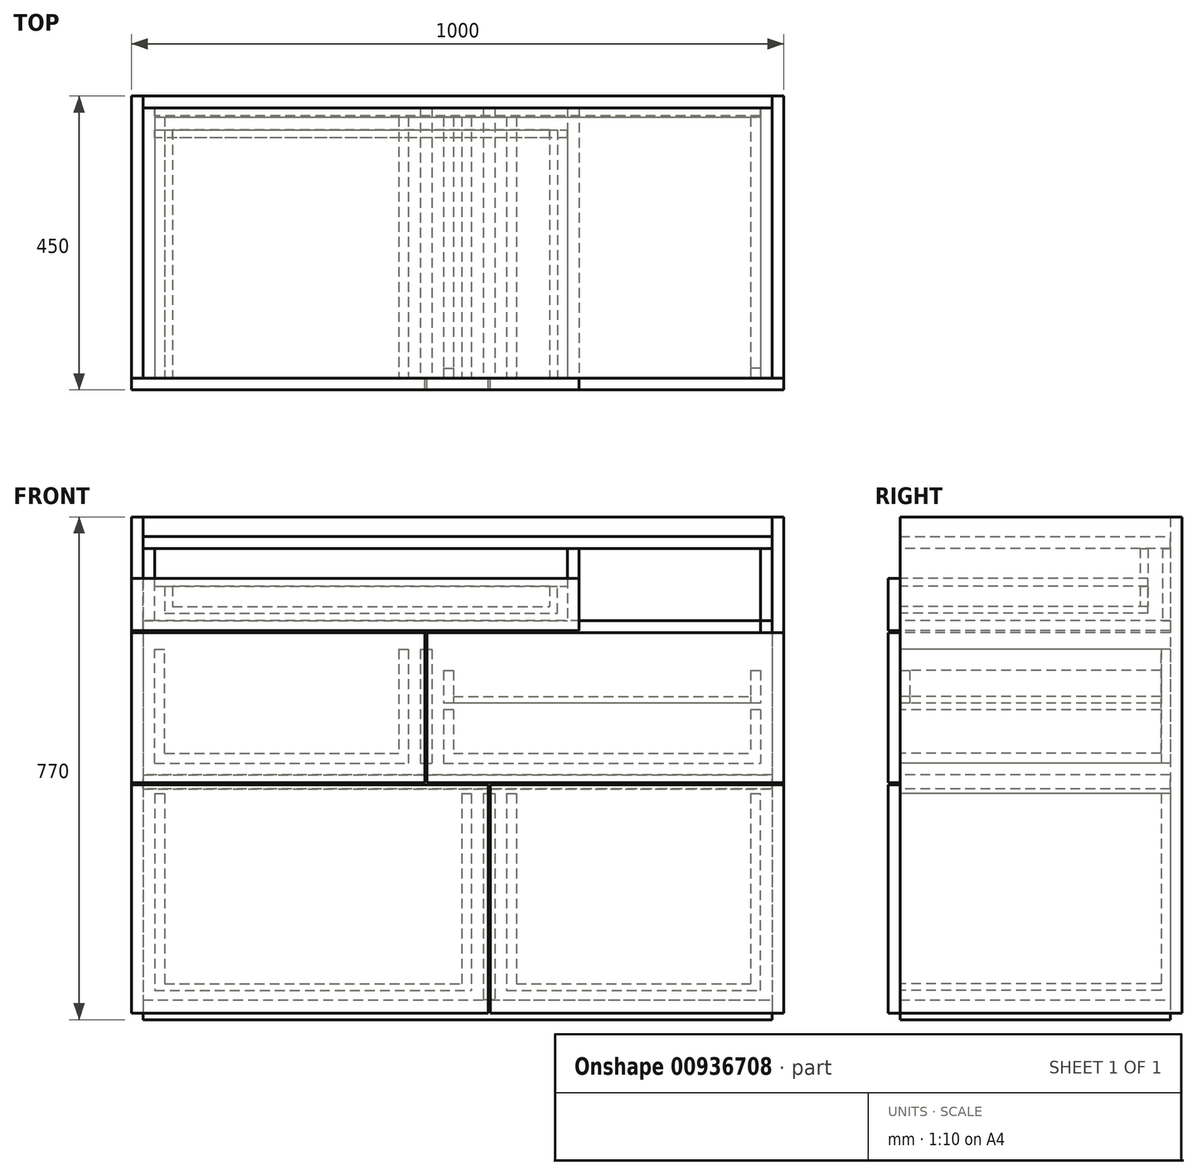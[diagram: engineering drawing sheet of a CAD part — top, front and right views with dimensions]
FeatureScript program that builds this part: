
annotation { "Feature Type Name" : "Feature", "Feature Type Description" : "" }
export const myFeature = defineFeature(function(context is Context, id is Id, definition is map)
    precondition{}
    {
        {
            var Q0;
            Q0=qCreatedBy(makeId("Top.planeOp"),FACE);
            var sketch = newSketch(context, id + "F0", { "sketchPlane" : qUnion([Q0])});
            skLineSegment(sketch, "E0.bottom", {"start": v(0, 0) * mm, "end": v(1000, 0) * mm});
            skLineSegment(sketch, "E0.top", {"start": v(0, 432) * mm, "end": v(1000, 432) * mm});
            skLineSegment(sketch, "E0.left", {"start": v(0, 0) * mm, "end": v(0, 432) * mm});
            skLineSegment(sketch, "E0.right", {"start": v(1000, 0) * mm, "end": v(1000, 432) * mm});
            skLineSegment(sketch, "E1.0", {"start": v(18, 0) * mm, "end": v(18, 432) * mm});
            skLineSegment(sketch, "E2", {"start": v(500, 455.77) * mm, "end": v(500, 504.04) * mm, "construction": true});
            skPoint(sketch, "E2.startSnap0", {"position": v(500, 432) * mm});
            skLineSegment(sketch, "E3.MirrorCS", {"start": v(982, 0) * mm, "end": v(982, 432) * mm});
            skLineSegment(sketch, "E4", {"start": v(1025.2, 216) * mm, "end": v(1096.23, 216) * mm, "construction": true});
            skPoint(sketch, "E4.startSnap0", {"position": v(1000, 216) * mm});
            skLineSegment(sketch, "E5.0", {"start": v(0, 414) * mm, "end": v(1000, 414) * mm});
            skSolve(sketch);
        }
        {
            var Q0;
            {var subQ0=sQuery(id+"F0.wireOp",EDGE,"E0.left");var subQ1=sQuery(id+"F0.wireOp",EDGE,"E0.bottom");var subQ2=makeQuery(id+"F0.imprint","INTERSECT",VERTEX,{"derivedFrom":[subQ1,subQ0]});Q0=makeQuery(id+"F0.imprint","IMPRINT",FACE,{"disambiguationData":[TD([[makeQuery(id+"F0.imprint","IMPRINT",EDGE,{"disambiguationData":[TD([[subQ2,-1.0]])],"derivedFrom":subQ1}),1.0]])]});}
            var Q1;
            {var subQ0=sQuery(id+"F0.wireOp",EDGE,"E0.left");var subQ1=sQuery(id+"F0.wireOp",EDGE,"E0.top");var subQ2=makeQuery(id+"F0.imprint","INTERSECT",VERTEX,{"derivedFrom":[subQ1,subQ0]});Q1=makeQuery(id+"F0.imprint","IMPRINT",FACE,{"disambiguationData":[TD([[makeQuery(id+"F0.imprint","IMPRINT",EDGE,{"disambiguationData":[TD([[subQ2,-1.0]])],"derivedFrom":subQ1}),-1.0]])]});}
            var Q2;
            {var subQ0=sQuery(id+"F0.wireOp",EDGE,"E0.right");var subQ1=sQuery(id+"F0.wireOp",EDGE,"E0.bottom");var subQ2=makeQuery(id+"F0.imprint","INTERSECT",VERTEX,{"derivedFrom":[subQ1,subQ0]});Q2=makeQuery(id+"F0.imprint","IMPRINT",FACE,{"disambiguationData":[TD([[makeQuery(id+"F0.imprint","IMPRINT",EDGE,{"disambiguationData":[TD([[subQ2,1.0]])],"derivedFrom":subQ1}),1.0]])]});}
            var Q3;
            {var subQ0=sQuery(id+"F0.wireOp",EDGE,"E0.right");var subQ1=sQuery(id+"F0.wireOp",EDGE,"E0.top");var subQ2=makeQuery(id+"F0.imprint","INTERSECT",VERTEX,{"derivedFrom":[subQ1,subQ0]});Q3=makeQuery(id+"F0.imprint","IMPRINT",FACE,{"disambiguationData":[TD([[makeQuery(id+"F0.imprint","IMPRINT",EDGE,{"disambiguationData":[TD([[subQ2,1.0]])],"derivedFrom":subQ1}),-1.0]])]});}
            extrude(context, id + "F1", {"entities" : qUnion([Q0, Q1, Q2, Q3]), "depth" : 760 * mm, "offsetDistance" : 25 * mm});
        }
        {
            var Q0;
            {var subQ0=sQuery(id+"F0.wireOp",EDGE,"E1.0");var subQ1=sQuery(id+"F0.wireOp",EDGE,"E0.top");var subQ2=makeQuery(id+"F0.imprint","INTERSECT",VERTEX,{"derivedFrom":[subQ1,subQ0]});Q0=makeQuery(id+"F0.imprint","IMPRINT",FACE,{"disambiguationData":[TD([[makeQuery(id+"F0.imprint","IMPRINT",EDGE,{"disambiguationData":[TD([[subQ2,-1.0]])],"derivedFrom":subQ1}),-1.0]])]});}
            var Q1;
            Q1=makeQuery(id+"F1.opExtrude","CAP_FACE",FACE,{"disambiguationData":[OSD([sQuery(id+"F0.wireOp",EDGE,"E0.bottom"),sQuery(id+"F0.wireOp",EDGE,"E0.top"),sQuery(id+"F0.wireOp",EDGE,"E0.left"),sQuery(id+"F0.wireOp",EDGE,"E1.0")])],"isStart":false});
            extrude(context, id + "F2", {"entities" : qUnion([Q0]), "endBound" : BoundingType.UP_TO_SURFACE, "depth" : 25 * mm, "endBoundEntityFace" : qUnion([Q1]), "offsetDistance" : 25 * mm});
        }
        {
            var Q0;
            {var subQ0=sQuery(id+"F0.wireOp",EDGE,"E1.0");var subQ1=sQuery(id+"F0.wireOp",EDGE,"E0.bottom");var subQ2=makeQuery(id+"F0.imprint","INTERSECT",VERTEX,{"derivedFrom":[subQ1,subQ0]});Q0=makeQuery(id+"F0.imprint","IMPRINT",FACE,{"disambiguationData":[TD([[makeQuery(id+"F0.imprint","IMPRINT",EDGE,{"disambiguationData":[TD([[subQ2,-1.0]])],"derivedFrom":subQ1}),1.0]])]});}
            extrude(context, id + "F3", {"entities" : qUnion([Q0]), "depth" : 20 * mm, "offsetDistance" : 25 * mm, "hasSecondDirection" : true, "secondDirectionOppositeDirection" : true, "secondDirectionDepth" : 10 * mm});
        }
        {
            var Q0;
            Q0=makeQuery(id+"F1.opExtrude","CAP_FACE",FACE,{"disambiguationData":[OSD([sQuery(id+"F0.wireOp",EDGE,"E0.bottom"),sQuery(id+"F0.wireOp",EDGE,"E0.top"),sQuery(id+"F0.wireOp",EDGE,"E0.left"),sQuery(id+"F0.wireOp",EDGE,"E1.0")])],"isStart":false});
            var sketch = newSketch(context, id + "F4", { "sketchPlane" : qUnion([Q0])});
            skLineSegment(sketch, "E6.bottom", {"start": v(0, 432) * mm, "end": v(1000, 432) * mm});
            skLineSegment(sketch, "E6.top", {"start": v(0, 0) * mm, "end": v(1000, 0) * mm});
            skLineSegment(sketch, "E6.left", {"start": v(0, 432) * mm, "end": v(0, 0) * mm});
            skLineSegment(sketch, "E6.right", {"start": v(1000, 432) * mm, "end": v(1000, 0) * mm});
            skLineSegment(sketch, "E7.bottom", {"start": v(18, 0) * mm, "end": v(982, 0) * mm});
            skLineSegment(sketch, "E7.top", {"start": v(18, 414) * mm, "end": v(982, 414) * mm});
            skLineSegment(sketch, "E7.left", {"start": v(18, 0) * mm, "end": v(18, 414) * mm});
            skLineSegment(sketch, "E7.right", {"start": v(982, 0) * mm, "end": v(982, 414) * mm});
            skLineSegment(sketch, "E8", {"start": v(668, 414) * mm, "end": v(668, 0) * mm});
            skLineSegment(sketch, "E9", {"start": v(18, 300) * mm, "end": v(668, 300) * mm});
            skLineSegment(sketch, "E10", {"start": v(55.2, 414) * mm, "end": v(55.2, -186) * mm, "construction": true});
            skLineSegment(sketch, "E11", {"start": v(-81.86, 114) * mm, "end": v(55.2, 114) * mm, "construction": true});
            skLineSegment(sketch, "E12", {"start": v(55.2, 0) * mm, "end": v(-78.13, 0) * mm, "construction": true});
            skLineSegment(sketch, "E13", {"start": v(55.2, -186) * mm, "end": v(-68.9, -186) * mm, "construction": true});
            skSolve(sketch);
        }
        {
            var Q0;
            {var subQ0=sQuery(id+"F4.wireOp",EDGE,"E7.right");Q0=makeQuery(id+"F4.imprint","IMPRINT",FACE,{"disambiguationData":[TD([[makeQuery(id+"F4.imprint","IMPRINT",EDGE,{"derivedFrom":subQ0}),1.0]])]});}
            var Q1;
            {var subQ5=sQuery(id+"F4.wireOp",EDGE,"E9");Q1=makeQuery(id+"F4.imprint","IMPRINT",FACE,{"disambiguationData":[TD([[makeQuery(id+"F4.imprint","IMPRINT",EDGE,{"derivedFrom":subQ5}),-1.0]])]});}
            var Q2;
            {var subQ5=sQuery(id+"F4.wireOp",EDGE,"E9");Q2=makeQuery(id+"F4.imprint","IMPRINT",FACE,{"disambiguationData":[TD([[makeQuery(id+"F4.imprint","IMPRINT",EDGE,{"derivedFrom":subQ5}),1.0]])]});}
            extrude(context, id + "F5", {"entities" : qUnion([Q0, Q1, Q2]), "oppositeDirection" : true, "depth" : 18 * mm, "offsetDistance" : 25 * mm});
        }
        {
            var Q0;
            Q0=makeQuery(id+"FaU98XOoRjI6tdl_2.opExtrude","SWEPT_BODY",BODY,{"disambiguationData":[OSD([sQuery(id+"F4.wireOp",EDGE,"E7.bottom"),sQuery(id+"F4.wireOp",EDGE,"E7.top"),sQuery(id+"F4.wireOp",EDGE,"E7.left"),sQuery(id+"F4.wireOp",EDGE,"E8")])]});
            var Q1;
            Q1=makeQuery(id+"F5.opExtrude","SWEPT_BODY",BODY,{"disambiguationData":[OSD([sQuery(id+"F4.wireOp",EDGE,"E7.bottom"),sQuery(id+"F4.wireOp",EDGE,"E7.top"),sQuery(id+"F4.wireOp",EDGE,"E7.right"),sQuery(id+"F4.wireOp",EDGE,"E8")])]});
            transform(context, id + "F6", {"entities" : qUnion([Q0, Q1]), "transformType" : TransformType.TRANSLATION_3D, "dx" : 0 * mm, "dy" : 0 * mm, "dz" : -30 * mm, "makeCopy" : false});
        }
        {
            var Q0;
            {var subQ0=sQuery(id+"F0.wireOp",EDGE,"E0.bottom");Q0=makeQuery(id+"F1.opExtrude","SWEPT_FACE",FACE,{"disambiguationData":[OSD([subQ0]),TDD([makeQuery(id+"F0.imprint","IMPRINT",EDGE,{"disambiguationData":[TD([[makeQuery(id+"F0.imprint","INTERSECT",VERTEX,{"derivedFrom":[subQ0,sQuery(id+"F0.wireOp",EDGE,"E0.left")]}),-1.0]])],"derivedFrom":subQ0})])]});}
            var sketch = newSketch(context, id + "F7", { "sketchPlane" : qUnion([Q0])});
            skLineSegment(sketch, "E14.bottom", {"start": v(0, 730) * mm, "end": v(668, 730) * mm});
            skLineSegment(sketch, "E14.top", {"start": v(0, 586) * mm, "end": v(668, 586) * mm});
            skLineSegment(sketch, "E14.left", {"start": v(0, 730) * mm, "end": v(0, 586) * mm});
            skLineSegment(sketch, "E14.right", {"start": v(668, 730) * mm, "end": v(668, 586) * mm});
            skLineSegment(sketch, "E15.bottom", {"start": v(1000, 583) * mm, "end": v(756, 583) * mm});
            skLineSegment(sketch, "E15.top", {"start": v(1000, 353) * mm, "end": v(756, 353) * mm});
            skLineSegment(sketch, "E15.left", {"start": v(1000, 583) * mm, "end": v(1000, 353) * mm});
            skLineSegment(sketch, "E15.right", {"start": v(756, 583) * mm, "end": v(756, 353) * mm});
            skLineSegment(sketch, "E16.bottom", {"start": v(753, 583) * mm, "end": v(453, 583) * mm});
            skLineSegment(sketch, "E16.top", {"start": v(753, 353) * mm, "end": v(453, 353) * mm});
            skLineSegment(sketch, "E16.left", {"start": v(753, 583) * mm, "end": v(753, 353) * mm});
            skLineSegment(sketch, "E16.right", {"start": v(453, 583) * mm, "end": v(453, 353) * mm});
            skLineSegment(sketch, "E17.bottom", {"start": v(450, 583) * mm, "end": v(0, 583) * mm});
            skLineSegment(sketch, "E17.top", {"start": v(450, 353) * mm, "end": v(0, 353) * mm});
            skLineSegment(sketch, "E17.left", {"start": v(450, 583) * mm, "end": v(450, 353) * mm});
            skLineSegment(sketch, "E17.right", {"start": v(0, 583) * mm, "end": v(0, 353) * mm});
            skLineSegment(sketch, "E18.bottom", {"start": v(671, 730) * mm, "end": v(1000, 730) * mm});
            skLineSegment(sketch, "E18.top", {"start": v(671, 586) * mm, "end": v(1000, 586) * mm});
            skLineSegment(sketch, "E18.left", {"start": v(671, 730) * mm, "end": v(671, 586) * mm});
            skLineSegment(sketch, "E18.right", {"start": v(1000, 730) * mm, "end": v(1000, 586) * mm});
            skLineSegment(sketch, "E19", {"start": v(668, 658) * mm, "end": v(671, 658) * mm, "construction": true});
            skLineSegment(sketch, "E20", {"start": v(1108.22, 586) * mm, "end": v(1108.22, 583) * mm, "construction": true});
            skLineSegment(sketch, "E21", {"start": v(756, 468) * mm, "end": v(753, 468) * mm, "construction": true});
            skLineSegment(sketch, "E22", {"start": v(453, 468) * mm, "end": v(450, 468) * mm, "construction": true});
            skLineSegment(sketch, "E23.bottom", {"start": v(0, 0) * mm, "end": v(244, 0) * mm});
            skLineSegment(sketch, "E23.top", {"start": v(0, 350) * mm, "end": v(244, 350) * mm});
            skLineSegment(sketch, "E23.left", {"start": v(0, 0) * mm, "end": v(0, 350) * mm});
            skLineSegment(sketch, "E23.right", {"start": v(244, 0) * mm, "end": v(244, 350) * mm});
            skLineSegment(sketch, "E24.bottom", {"start": v(247, 350) * mm, "end": v(547, 350) * mm});
            skLineSegment(sketch, "E24.top", {"start": v(247, 0) * mm, "end": v(547, 0) * mm});
            skLineSegment(sketch, "E24.left", {"start": v(247, 350) * mm, "end": v(247, 0) * mm});
            skLineSegment(sketch, "E24.right", {"start": v(547, 350) * mm, "end": v(547, 0) * mm});
            skLineSegment(sketch, "E25.bottom", {"start": v(550, 350) * mm, "end": v(1000, 350) * mm});
            skLineSegment(sketch, "E25.top", {"start": v(550, 0) * mm, "end": v(1000, 0) * mm});
            skLineSegment(sketch, "E25.left", {"start": v(550, 350) * mm, "end": v(550, 0) * mm});
            skLineSegment(sketch, "E25.right", {"start": v(1000, 350) * mm, "end": v(1000, 0) * mm});
            skLineSegment(sketch, "E26", {"start": v(122, 353) * mm, "end": v(122, 350) * mm, "construction": true});
            skPoint(sketch, "E26.startSnap0", {"position": v(122, 350) * mm});
            skLineSegment(sketch, "E27", {"start": v(244, 175) * mm, "end": v(247, 175) * mm, "construction": true});
            skLineSegment(sketch, "E28", {"start": v(550, 175) * mm, "end": v(547, 175) * mm, "construction": true});
            skLineSegment(sketch, "E29.bottom", {"start": v(671, 586) * mm, "end": v(982, 586) * mm});
            skLineSegment(sketch, "E29.top", {"start": v(671, 604) * mm, "end": v(982, 604) * mm});
            skLineSegment(sketch, "E29.left", {"start": v(671, 586) * mm, "end": v(671, 604) * mm});
            skLineSegment(sketch, "E29.right", {"start": v(982, 586) * mm, "end": v(982, 604) * mm});
            skLineSegment(sketch, "E30", {"start": v(668, 712) * mm, "end": v(0, 712) * mm});
            skLineSegment(sketch, "E31", {"start": v(450, 583) * mm, "end": v(453, 583) * mm});
            skLineSegment(sketch, "E32", {"start": v(450, 353) * mm, "end": v(453, 353) * mm});
            skLineSegment(sketch, "E33", {"start": v(547, 350) * mm, "end": v(550, 350) * mm});
            skLineSegment(sketch, "E34", {"start": v(547, 0) * mm, "end": v(550, 0) * mm});
            skLineSegment(sketch, "E35", {"start": v(753, 583) * mm, "end": v(756, 583) * mm});
            skLineSegment(sketch, "E36", {"start": v(753, 353) * mm, "end": v(756, 353) * mm});
            skLineSegment(sketch, "E37", {"start": v(244, 350) * mm, "end": v(247, 350) * mm});
            skLineSegment(sketch, "E38", {"start": v(244, 0) * mm, "end": v(247, 0) * mm});
            skLineSegment(sketch, "E39", {"start": v(0, 666) * mm, "end": v(668, 666) * mm});
            skSolve(sketch);
        }
        {
            var Q0;
            {var subQ0=sQuery(id+"F7.wireOp",EDGE,"E17.left");Q0=makeQuery(id+"F7.imprint","IMPRINT",FACE,{"disambiguationData":[TD([[makeQuery(id+"F7.imprint","IMPRINT",EDGE,{"derivedFrom":subQ0}),-1.0]])]});}
            var Q1;
            Q1=makeQuery(id+"F7.imprint","IMPRINT",FACE,{"disambiguationData":[TD([[makeQuery(id+"F7.imprint","IMPRINT",EDGE,{"derivedFrom":sQuery(id+"F7.wireOp",EDGE,"E16.bottom")}),1.0]])]});
            var Q2;
            Q2=makeQuery(id+"F7.imprint","IMPRINT",FACE,{"disambiguationData":[TD([[makeQuery(id+"F7.imprint","IMPRINT",EDGE,{"derivedFrom":sQuery(id+"F7.wireOp",EDGE,"E15.bottom")}),1.0]])]});
            var Q3;
            Q3=makeQuery(id+"F7.imprint","IMPRINT",FACE,{"disambiguationData":[TD([[makeQuery(id+"F7.imprint","IMPRINT",EDGE,{"derivedFrom":sQuery(id+"F7.wireOp",EDGE,"E25.bottom")}),-1.0]])]});
            var Q4;
            Q4=makeQuery(id+"F7.imprint","IMPRINT",FACE,{"disambiguationData":[TD([[makeQuery(id+"F7.imprint","IMPRINT",EDGE,{"derivedFrom":sQuery(id+"F7.wireOp",EDGE,"E24.bottom")}),-1.0]])]});
            var Q5;
            {var subQ3=sQuery(id+"F7.wireOp",EDGE,"E23.right");Q5=makeQuery(id+"F7.imprint","IMPRINT",FACE,{"disambiguationData":[TD([[makeQuery(id+"F7.imprint","IMPRINT",EDGE,{"derivedFrom":subQ3}),1.0]])]});}
            var Q6;
            {var subQ0=sQuery(id+"F7.wireOp",EDGE,"E17.right");Q6=makeQuery(id+"F7.imprint","IMPRINT",FACE,{"disambiguationData":[TD([[makeQuery(id+"F7.imprint","IMPRINT",EDGE,{"derivedFrom":subQ0}),1.0]])]});}
            var Q7;
            {var subQ0=sQuery(id+"F7.wireOp",EDGE,"E23.left");Q7=makeQuery(id+"F7.imprint","IMPRINT",FACE,{"disambiguationData":[TD([[makeQuery(id+"F7.imprint","IMPRINT",EDGE,{"derivedFrom":subQ0}),1.0]])]});}
            var Q8;
            {var subQ0=sQuery(id+"F7.wireOp",EDGE,"E14.right");var subQ1=sQuery(id+"F7.wireOp",EDGE,"E14.top");var subQ2=makeQuery(id+"F7.imprint","INTERSECT",VERTEX,{"derivedFrom":[subQ1,subQ0]});Q8=makeQuery(id+"F7.imprint","IMPRINT",FACE,{"disambiguationData":[TD([[makeQuery(id+"F7.imprint","IMPRINT",EDGE,{"disambiguationData":[TD([[subQ2,1.0]])],"derivedFrom":subQ0}),-1.0]])]});}
            var Q9;
            Q9=makeQuery(id+"F7.imprint","IMPRINT",FACE,{"disambiguationData":[TD([[makeQuery(id+"F7.imprint","IMPRINT",EDGE,{"derivedFrom":sQuery(id+"F7.wireOp",EDGE,"E23.right")}),-1.0]])]});
            var Q10;
            Q10=makeQuery(id+"F7.imprint","IMPRINT",FACE,{"disambiguationData":[TD([[makeQuery(id+"F7.imprint","IMPRINT",EDGE,{"derivedFrom":sQuery(id+"F7.wireOp",EDGE,"E15.right")}),-1.0]])]});
            var Q11;
            {var subQ0=sQuery(id+"F7.wireOp",EDGE,"E14.left");var subQ6=sQuery(id+"F7.wireOp",EDGE,"E39");var subQ8=makeQuery(id+"F7.imprint","INTERSECT",VERTEX,{"derivedFrom":[subQ0,subQ6]});Q11=makeQuery(id+"F7.imprint","IMPRINT",FACE,{"disambiguationData":[TD([[makeQuery(id+"F7.imprint","IMPRINT",EDGE,{"disambiguationData":[TD([[subQ8,-1.0]])],"derivedFrom":subQ6}),-1.0]])]});}
            extrude(context, id + "F8", {"entities" : qUnion([Q0, Q1, Q2, Q3, Q4, Q5, Q6, Q7, Q8, Q9, Q10, Q11]), "depth" : 18 * mm, "offsetDistance" : 25 * mm});
        }
        {
            var Q0;
            Q0=makeQuery(id+"F8.opExtrude","CAP_FACE",FACE,{"disambiguationData":[OSD([sQuery(id+"F7.wireOp",EDGE,"E14.bottom"),sQuery(id+"F7.wireOp",EDGE,"E14.top"),sQuery(id+"F7.wireOp",EDGE,"E14.left"),sQuery(id+"F7.wireOp",EDGE,"E14.right")])],"isStart":true});
            var sketch = newSketch(context, id + "F9", { "sketchPlane" : qUnion([Q0])});
            skLineSegment(sketch, "E40.bottom", {"start": v(-18, 583) * mm, "end": v(-982, 583) * mm});
            skLineSegment(sketch, "E40.top", {"start": v(-18, 565) * mm, "end": v(-982, 565) * mm});
            skLineSegment(sketch, "E40.left", {"start": v(-18, 583) * mm, "end": v(-18, 565) * mm});
            skLineSegment(sketch, "E40.right", {"start": v(-982, 583) * mm, "end": v(-982, 565) * mm});
            skLineSegment(sketch, "E41.bottom", {"start": v(-18, 365) * mm, "end": v(-982, 365) * mm});
            skLineSegment(sketch, "E41.top", {"start": v(-18, 343.75) * mm, "end": v(-982, 343.75) * mm});
            skLineSegment(sketch, "E41.left", {"start": v(-18, 365) * mm, "end": v(-18, 343.75) * mm});
            skLineSegment(sketch, "E41.right", {"start": v(-982, 365) * mm, "end": v(-982, 343.75) * mm});
            skLineSegment(sketch, "E42.bottom", {"start": v(-982, 565) * mm, "end": v(-964, 565) * mm});
            skLineSegment(sketch, "E42.top", {"start": v(-982, 365) * mm, "end": v(-964, 365) * mm});
            skLineSegment(sketch, "E42.left", {"start": v(-982, 565) * mm, "end": v(-982, 365) * mm});
            skLineSegment(sketch, "E42.right", {"start": v(-964, 565) * mm, "end": v(-964, 365) * mm});
            skLineSegment(sketch, "E43.bottom", {"start": v(-460.5, 565) * mm, "end": v(-442.5, 565) * mm});
            skLineSegment(sketch, "E43.top", {"start": v(-460.5, 365) * mm, "end": v(-442.5, 365) * mm});
            skLineSegment(sketch, "E43.left", {"start": v(-460.5, 565) * mm, "end": v(-460.5, 365) * mm});
            skLineSegment(sketch, "E43.right", {"start": v(-442.5, 565) * mm, "end": v(-442.5, 365) * mm});
            skLineSegment(sketch, "E44.bottom", {"start": v(-557.18, 343.75) * mm, "end": v(-539.18, 343.75) * mm});
            skLineSegment(sketch, "E44.top", {"start": v(-557.18, 20) * mm, "end": v(-539.18, 20) * mm});
            skLineSegment(sketch, "E44.left", {"start": v(-557.18, 343.75) * mm, "end": v(-557.18, 20) * mm});
            skLineSegment(sketch, "E44.right", {"start": v(-539.18, 343.75) * mm, "end": v(-539.18, 20) * mm});
            skLineSegment(sketch, "E45.bottom", {"start": v(-36, 343.75) * mm, "end": v(-18, 343.75) * mm});
            skLineSegment(sketch, "E45.top", {"start": v(-36, 20) * mm, "end": v(-18, 20) * mm});
            skLineSegment(sketch, "E45.left", {"start": v(-36, 343.75) * mm, "end": v(-36, 20) * mm});
            skLineSegment(sketch, "E45.right", {"start": v(-18, 343.75) * mm, "end": v(-18, 20) * mm});
            skLineSegment(sketch, "E46", {"start": v(-548.18, 289.25) * mm, "end": v(-548.18, 277.23) * mm, "construction": true});
            skPoint(sketch, "E47", {"position": v(-548.18, 20) * mm});
            skPoint(sketch, "E48", {"position": v(-27, 20) * mm});
            skPoint(sketch, "E49", {"position": v(-973, 365) * mm});
            skPoint(sketch, "E50", {"position": v(-451.5, 365) * mm});
            skLineSegment(sketch, "E51.bottom", {"start": v(-686, 712) * mm, "end": v(-668, 712) * mm});
            skLineSegment(sketch, "E51.left", {"start": v(-686, 712) * mm, "end": v(-686, 583) * mm});
            skLineSegment(sketch, "E51.right", {"start": v(-668, 712) * mm, "end": v(-668, 583) * mm});
            skPoint(sketch, "E52", {"position": v(-677, 563.5) * mm});
            skLineSegment(sketch, "E53.bottom", {"start": v(-982, 583) * mm, "end": v(-964, 583) * mm});
            skLineSegment(sketch, "E53.top", {"start": v(-982, 712) * mm, "end": v(-964, 712) * mm});
            skLineSegment(sketch, "E53.left", {"start": v(-982, 583) * mm, "end": v(-982, 712) * mm});
            skLineSegment(sketch, "E53.right", {"start": v(-964, 583) * mm, "end": v(-964, 712) * mm});
            skLineSegment(sketch, "E54.bottom", {"start": v(-36, 365) * mm, "end": v(-51, 365) * mm});
            skLineSegment(sketch, "E54.top", {"start": v(-36, 565) * mm, "end": v(-51, 565) * mm});
            skLineSegment(sketch, "E54.left", {"start": v(-36, 365) * mm, "end": v(-36, 565) * mm});
            skLineSegment(sketch, "E54.right", {"start": v(-51, 365) * mm, "end": v(-51, 565) * mm});
            skLineSegment(sketch, "E55.0", {"start": v(-949, 557.5) * mm, "end": v(-949, 383) * mm});
            skLineSegment(sketch, "E56.0", {"start": v(-478.5, 557.5) * mm, "end": v(-478.5, 379.75) * mm});
            skLineSegment(sketch, "E57.0", {"start": v(-424.5, 580.07) * mm, "end": v(-424.5, 383) * mm});
            skLineSegment(sketch, "E58", {"start": v(-949, 343.75) * mm, "end": v(-949, 20) * mm});
            skLineSegment(sketch, "E59", {"start": v(-51, 343.75) * mm, "end": v(-51, 20) * mm});
            skLineSegment(sketch, "E60", {"start": v(-36, 35) * mm, "end": v(-949, 35) * mm});
            skLineSegment(sketch, "E61.0", {"start": v(-36, 45) * mm, "end": v(-949, 45) * mm});
            skLineSegment(sketch, "E62.0", {"start": v(-36, 383) * mm, "end": v(-964, 383) * mm});
            skLineSegment(sketch, "E63", {"start": v(-949, 35) * mm, "end": v(-964, 35) * mm});
            skLineSegment(sketch, "E64", {"start": v(-964, 35) * mm, "end": v(-964, 343.75) * mm});
            skLineSegment(sketch, "E65", {"start": v(-949, 45) * mm, "end": v(-964, 45) * mm});
            skLineSegment(sketch, "E66.0", {"start": v(-521.18, 343.75) * mm, "end": v(-521.18, 35) * mm});
            skLineSegment(sketch, "E67.0", {"start": v(-575.18, 343.75) * mm, "end": v(-575.18, 35) * mm});
            skLineSegment(sketch, "E68.0", {"start": v(-409.5, 580.07) * mm, "end": v(-409.5, 383) * mm});
            skLineSegment(sketch, "E69.0", {"start": v(-493.5, 557.5) * mm, "end": v(-493.5, 383) * mm});
            skLineSegment(sketch, "E70.0", {"start": v(-506.18, 343.75) * mm, "end": v(-506.18, 35) * mm});
            skLineSegment(sketch, "E71.0", {"start": v(-590.18, 343.75) * mm, "end": v(-590.18, 35) * mm});
            skLineSegment(sketch, "E72.0", {"start": v(-18, 336.25) * mm, "end": v(-982, 336.25) * mm});
            skLineSegment(sketch, "E73.0", {"start": v(-18, 557.5) * mm, "end": v(-982, 557.5) * mm});
            skLineSegment(sketch, "E74.0", {"start": v(-36, 398) * mm, "end": v(-964, 398) * mm});
            skLineSegment(sketch, "E75.top", {"start": v(118.2, 343.75) * mm, "end": v(882.2, 343.75) * mm});
            skLineSegment(sketch, "E75.left", {"start": v(118.2, 361.75) * mm, "end": v(118.2, 343.75) * mm});
            skLineSegment(sketch, "E75.right", {"start": v(882.2, 361.75) * mm, "end": v(882.2, 343.75) * mm});
            skLineSegment(sketch, "E76.bottom", {"start": v(118.2, 343.75) * mm, "end": v(136.2, 343.75) * mm});
            skLineSegment(sketch, "E76.top", {"start": v(118.2, 20) * mm, "end": v(136.2, 20) * mm});
            skLineSegment(sketch, "E76.left", {"start": v(118.2, 343.75) * mm, "end": v(118.2, 20) * mm});
            skLineSegment(sketch, "E76.right", {"start": v(136.2, 343.75) * mm, "end": v(136.2, 20) * mm});
            skPoint(sketch, "E77", {"position": v(118.2, 352.75) * mm});
            skPoint(sketch, "E78", {"position": v(127.2, 343.75) * mm});
            skLineSegment(sketch, "E79.bottom", {"start": v(882.2, 343.75) * mm, "end": v(864.2, 343.75) * mm});
            skLineSegment(sketch, "E79.top", {"start": v(882.2, 20) * mm, "end": v(864.2, 20) * mm});
            skLineSegment(sketch, "E79.left", {"start": v(882.2, 343.75) * mm, "end": v(882.2, 20) * mm});
            skLineSegment(sketch, "E79.right", {"start": v(864.2, 343.75) * mm, "end": v(864.2, 20) * mm});
            skLineSegment(sketch, "E80.bottom", {"start": v(864.2, 35) * mm, "end": v(136.2, 35) * mm});
            skLineSegment(sketch, "E80.top", {"start": v(864.2, 45) * mm, "end": v(136.2, 45) * mm});
            skLineSegment(sketch, "E80.left", {"start": v(864.2, 35) * mm, "end": v(864.2, 45) * mm});
            skLineSegment(sketch, "E80.right", {"start": v(136.2, 35) * mm, "end": v(136.2, 45) * mm});
            skLineSegment(sketch, "E81", {"start": v(864.2, 35) * mm, "end": v(882.2, 35) * mm});
            skLineSegment(sketch, "E82", {"start": v(136.2, 35) * mm, "end": v(118.2, 35) * mm});
            skLineSegment(sketch, "E83", {"start": v(361.6, 35) * mm, "end": v(361.6, 20) * mm, "construction": true});
            skLineSegment(sketch, "E84.bottom", {"start": v(882.2, 303.75) * mm, "end": v(136.2, 303.75) * mm});
            skLineSegment(sketch, "E84.top", {"start": v(882.2, 253.75) * mm, "end": v(136.2, 253.75) * mm});
            skLineSegment(sketch, "E84.left", {"start": v(882.2, 303.75) * mm, "end": v(882.2, 253.75) * mm});
            skLineSegment(sketch, "E84.right", {"start": v(136.2, 303.75) * mm, "end": v(136.2, 253.75) * mm});
            skLineSegment(sketch, "E85.0", {"start": v(849.2, 342.5) * mm, "end": v(849.2, 20) * mm});
            skLineSegment(sketch, "E86.0", {"start": v(151.2, 342.5) * mm, "end": v(151.2, 20) * mm});
            skLineSegment(sketch, "E87", {"start": v(136.2, 235) * mm, "end": v(151.2, 235) * mm});
            skLineSegment(sketch, "E88", {"start": v(849.2, 235) * mm, "end": v(864.2, 235) * mm});
            skLineSegment(sketch, "E89.0", {"start": v(882.2, 263.75) * mm, "end": v(136.2, 263.75) * mm});
            skLineSegment(sketch, "E90", {"start": v(-521.18, 285) * mm, "end": v(-506.18, 285) * mm});
            skLineSegment(sketch, "E91", {"start": v(-51, 285) * mm, "end": v(-36, 285) * mm});
            skLineSegment(sketch, "E92", {"start": v(-575.18, 475) * mm, "end": v(-964, 475) * mm});
            skLineSegment(sketch, "E93", {"start": v(-575.18, 485) * mm, "end": v(-964, 485) * mm});
            skLineSegment(sketch, "E94", {"start": v(-575.18, 525) * mm, "end": v(-964, 525) * mm});
            skLineSegment(sketch, "E95", {"start": v(-575.18, 285) * mm, "end": v(-590.18, 285) * mm});
            skLineSegment(sketch, "E96", {"start": v(-949, 285) * mm, "end": v(-964, 285) * mm});
            skLineSegment(sketch, "E97", {"start": v(-668, 601) * mm, "end": v(-982, 601) * mm});
            skLineSegment(sketch, "E98.bottom", {"start": v(-18, 583) * mm, "end": v(-36, 583) * mm});
            skLineSegment(sketch, "E98.top", {"start": v(-18, 712) * mm, "end": v(-36, 712) * mm});
            skLineSegment(sketch, "E98.left", {"start": v(-18, 583) * mm, "end": v(-18, 712) * mm});
            skLineSegment(sketch, "E98.right", {"start": v(-36, 583) * mm, "end": v(-36, 712) * mm});
            skLineSegment(sketch, "E99.0", {"start": v(-18, 574) * mm, "end": v(-982, 574) * mm});
            skLineSegment(sketch, "E100", {"start": v(-668, 601) * mm, "end": v(-18, 601) * mm});
            skLineSegment(sketch, "E101", {"start": v(-575.18, 525) * mm, "end": v(-478.5, 525) * mm});
            skLineSegment(sketch, "E102", {"start": v(-575.18, 485) * mm, "end": v(-478.5, 485) * mm});
            skLineSegment(sketch, "E103", {"start": v(-575.18, 475) * mm, "end": v(-478.5, 475) * mm});
            skLineSegment(sketch, "E104", {"start": v(-964, 465) * mm, "end": v(-949, 465) * mm});
            skLineSegment(sketch, "E105", {"start": v(-493.5, 465) * mm, "end": v(-478.5, 465) * mm});
            skSolve(sketch);
        }
        {
            var Q0;
            {var subQ2=sQuery(id+"F9.wireOp",EDGE,"E41.left");Q0=makeQuery(id+"F9.imprint","IMPRINT",FACE,{"disambiguationData":[TD([[makeQuery(id+"F9.imprint","IMPRINT",EDGE,{"derivedFrom":subQ2}),-1.0]])]});}
            var Q1;
            {var subQ4=sQuery(id+"F9.wireOp",EDGE,"E53.bottom");Q1=makeQuery(id+"F9.imprint","IMPRINT",FACE,{"disambiguationData":[TD([[makeQuery(id+"F9.imprint","IMPRINT",EDGE,{"derivedFrom":subQ4}),-1.0]])]});}
            var Q2;
            {var subQ1=sQuery(id+"F9.wireOp",EDGE,"E40.bottom");var subQ3=sQuery(id+"F9.wireOp",EDGE,"E51.left");var subQ4=makeQuery(id+"F9.imprint","INTERSECT",VERTEX,{"derivedFrom":[subQ1,subQ3]});Q2=makeQuery(id+"F9.imprint","IMPRINT",FACE,{"disambiguationData":[TD([[makeQuery(id+"F9.imprint","IMPRINT",EDGE,{"disambiguationData":[TD([[subQ4,1.0]])],"derivedFrom":subQ3}),-1.0]])]});}
            var Q3;
            {var subQ2=sQuery(id+"F9.wireOp",EDGE,"E40.bottom");var subQ4=sQuery(id+"F9.wireOp",EDGE,"E51.left");var subQ5=makeQuery(id+"F9.imprint","INTERSECT",VERTEX,{"derivedFrom":[subQ2,subQ4]});Q3=makeQuery(id+"F9.imprint","IMPRINT",FACE,{"disambiguationData":[TD([[makeQuery(id+"F9.imprint","IMPRINT",EDGE,{"disambiguationData":[TD([[subQ5,1.0]])],"derivedFrom":subQ2}),-1.0]])]});}
            var Q4;
            {var subQ0=sQuery(id+"F9.wireOp",EDGE,"E53.bottom");Q4=makeQuery(id+"F9.imprint","IMPRINT",FACE,{"disambiguationData":[TD([[makeQuery(id+"F9.imprint","IMPRINT",EDGE,{"derivedFrom":subQ0}),1.0]])]});}
            var Q5;
            {var subQ3=sQuery(id+"F9.wireOp",EDGE,"E100");var subQ5=sQuery(id+"F9.wireOp",EDGE,"E98.right");var subQ6=makeQuery(id+"F9.imprint","INTERSECT",VERTEX,{"derivedFrom":[subQ5,subQ3]});Q5=makeQuery(id+"F9.imprint","IMPRINT",FACE,{"disambiguationData":[TD([[makeQuery(id+"F9.imprint","IMPRINT",EDGE,{"disambiguationData":[TD([[subQ6,1.0]])],"derivedFrom":subQ5}),1.0]])]});}
            var Q6;
            {var subQ0=sQuery(id+"F9.wireOp",EDGE,"E100");var subQ1=sQuery(id+"F9.wireOp",EDGE,"E98.left");var subQ2=makeQuery(id+"F9.imprint","INTERSECT",VERTEX,{"derivedFrom":[subQ1,subQ0]});Q6=makeQuery(id+"F9.imprint","IMPRINT",FACE,{"disambiguationData":[TD([[makeQuery(id+"F9.imprint","IMPRINT",EDGE,{"disambiguationData":[TD([[subQ2,1.0]])],"derivedFrom":subQ1}),1.0]])]});}
            var Q7;
            {var subQ0=sQuery(id+"F9.wireOp",EDGE,"E98.bottom");Q7=makeQuery(id+"F9.imprint","IMPRINT",FACE,{"disambiguationData":[TD([[makeQuery(id+"F9.imprint","IMPRINT",EDGE,{"derivedFrom":subQ0}),-1.0]])]});}
            var Q8;
            {var subQ3=sQuery(id+"F9.wireOp",EDGE,"E51.right");var subQ5=makeQuery(id+"F8.opExtrude","CAP_EDGE",EDGE,{"disambiguationData":[OSD([sQuery(id+"F7.wireOp",EDGE,"E14.top")])],"isStart":true});var subQ6=makeQuery(id+"F9.imprint","INTERSECT",VERTEX,{"derivedFrom":[subQ5,subQ3]});Q8=makeQuery(id+"F9.imprint","IMPRINT",FACE,{"disambiguationData":[TD([[makeQuery(id+"F9.imprint","IMPRINT",EDGE,{"disambiguationData":[TD([[subQ6,-1.0]])],"derivedFrom":subQ3}),1.0]])]});}
            var Q9;
            Q9=makeQuery(id+"F5.opExtrude","SWEPT_FACE",FACE,{"disambiguationData":[OSD([sQuery(id+"F4.wireOp",EDGE,"E7.top")])]});
            extrude(context, id + "F10", {"entities" : qUnion([Q0, Q1, Q2, Q3, Q4, Q5, Q6, Q7, Q8]), "endBound" : BoundingType.UP_TO_SURFACE, "depth" : 25 * mm, "endBoundEntityFace" : qUnion([Q9]), "offsetDistance" : 25 * mm});
        }
        {
            var Q0;
            Q0=makeQuery(id+"F9.imprint","IMPRINT",FACE,{"disambiguationData":[TD([[makeQuery(id+"F9.imprint","IMPRINT",EDGE,{"derivedFrom":sQuery(id+"F9.wireOp",EDGE,"E51.bottom")}),-1.0]])]});
            var Q1;
            Q1=makeQuery(id+"F9.imprint","IMPRINT",FACE,{"disambiguationData":[TD([[makeQuery(id+"F9.imprint","IMPRINT",EDGE,{"derivedFrom":sQuery(id+"F9.wireOp",EDGE,"E43.bottom")}),-1.0]])]});
            var Q2;
            Q2=makeQuery(id+"F9.imprint","IMPRINT",FACE,{"disambiguationData":[TD([[makeQuery(id+"F9.imprint","IMPRINT",EDGE,{"derivedFrom":sQuery(id+"F9.wireOp",EDGE,"E44.bottom")}),-1.0]])]});
            var Q3;
            {var subQ0=sQuery(id+"F9.wireOp",EDGE,"E73.0");var subQ1=sQuery(id+"F9.wireOp",EDGE,"E43.left");var subQ2=makeQuery(id+"F9.imprint","INTERSECT",VERTEX,{"derivedFrom":[subQ1,subQ0]});Q3=makeQuery(id+"F9.imprint","IMPRINT",FACE,{"disambiguationData":[TD([[makeQuery(id+"F9.imprint","IMPRINT",EDGE,{"disambiguationData":[TD([[subQ2,-1.0]])],"derivedFrom":subQ1}),1.0]])]});}
            var Q4;
            {var subQ0=sQuery(id+"F9.wireOp",EDGE,"E74.0");var subQ1=sQuery(id+"F9.wireOp",EDGE,"E43.left");var subQ2=makeQuery(id+"F9.imprint","INTERSECT",VERTEX,{"derivedFrom":[subQ1,subQ0]});Q4=makeQuery(id+"F9.imprint","IMPRINT",FACE,{"disambiguationData":[TD([[makeQuery(id+"F9.imprint","IMPRINT",EDGE,{"disambiguationData":[TD([[subQ2,-1.0]])],"derivedFrom":subQ1}),1.0]])]});}
            var Q5;
            {var subQ0=sQuery(id+"F9.wireOp",EDGE,"E43.top");Q5=makeQuery(id+"F9.imprint","IMPRINT",FACE,{"disambiguationData":[TD([[makeQuery(id+"F9.imprint","IMPRINT",EDGE,{"derivedFrom":subQ0}),1.0]])]});}
            var Q6;
            {var subQ0=sQuery(id+"F9.wireOp",EDGE,"E72.0");var subQ1=sQuery(id+"F9.wireOp",EDGE,"E44.left");var subQ2=makeQuery(id+"F9.imprint","INTERSECT",VERTEX,{"derivedFrom":[subQ1,subQ0]});Q6=makeQuery(id+"F9.imprint","IMPRINT",FACE,{"disambiguationData":[TD([[makeQuery(id+"F9.imprint","IMPRINT",EDGE,{"disambiguationData":[TD([[subQ2,-1.0]])],"derivedFrom":subQ1}),1.0]])]});}
            var Q7;
            {var subQ0=sQuery(id+"F9.wireOp",EDGE,"E60");var subQ1=sQuery(id+"F9.wireOp",EDGE,"E44.left");var subQ2=makeQuery(id+"F9.imprint","INTERSECT",VERTEX,{"derivedFrom":[subQ1,subQ0]});Q7=makeQuery(id+"F9.imprint","IMPRINT",FACE,{"disambiguationData":[TD([[makeQuery(id+"F9.imprint","IMPRINT",EDGE,{"disambiguationData":[TD([[subQ2,1.0]])],"derivedFrom":subQ1}),1.0]])]});}
            var Q8;
            {var subQ0=sQuery(id+"F9.wireOp",EDGE,"E44.top");Q8=makeQuery(id+"F9.imprint","IMPRINT",FACE,{"disambiguationData":[TD([[makeQuery(id+"F9.imprint","IMPRINT",EDGE,{"derivedFrom":subQ0}),1.0]])]});}
            var Q9;
            {var subQ0=sQuery(id+"F9.wireOp",EDGE,"E53.top");Q9=makeQuery(id+"F9.imprint","IMPRINT",FACE,{"disambiguationData":[TD([[makeQuery(id+"F9.imprint","IMPRINT",EDGE,{"derivedFrom":subQ0}),-1.0]])]});}
            var Q10;
            {var subQ0=sQuery(id+"F9.wireOp",EDGE,"E98.top");Q10=makeQuery(id+"F9.imprint","IMPRINT",FACE,{"disambiguationData":[TD([[makeQuery(id+"F9.imprint","IMPRINT",EDGE,{"derivedFrom":subQ0}),1.0]])]});}
            var Q11;
            {var subQ0=sQuery(id+"F9.wireOp",EDGE,"E100");var subQ1=sQuery(id+"F9.wireOp",EDGE,"E98.left");var subQ2=makeQuery(id+"F9.imprint","INTERSECT",VERTEX,{"derivedFrom":[subQ1,subQ0]});Q11=makeQuery(id+"F9.imprint","IMPRINT",FACE,{"disambiguationData":[TD([[makeQuery(id+"F9.imprint","IMPRINT",EDGE,{"disambiguationData":[TD([[subQ2,-1.0]])],"derivedFrom":subQ1}),1.0]])]});}
            var Q12;
            Q12=makeQuery(id+"F3.opExtrude","SWEPT_FACE",FACE,{"disambiguationData":[OSD([sQuery(id+"F0.wireOp",EDGE,"E5.0")])]});
            extrude(context, id + "F11", {"entities" : qUnion([Q0, Q1, Q2, Q3, Q4, Q5, Q6, Q7, Q8, Q9, Q10, Q11]), "endBound" : BoundingType.UP_TO_SURFACE, "depth" : 25 * mm, "endBoundEntityFace" : qUnion([Q12]), "offsetDistance" : 25 * mm});
        }
        {
            var Q0;
            Q0=makeQuery(id+"F2.opExtrude","SWEPT_FACE",FACE,{"disambiguationData":[OSD([sQuery(id+"F0.wireOp",EDGE,"E5.0")])]});
            var sketch = newSketch(context, id + "F12", { "sketchPlane" : qUnion([Q0])});
            skLineSegment(sketch, "E106.bottom", {"start": v(964, 712) * mm, "end": v(36, 712) * mm});
            skLineSegment(sketch, "E106.top", {"start": v(964, 601) * mm, "end": v(36, 601) * mm});
            skLineSegment(sketch, "E106.left", {"start": v(964, 712) * mm, "end": v(964, 601) * mm});
            skLineSegment(sketch, "E106.right", {"start": v(36, 712) * mm, "end": v(36, 601) * mm});
            skSolve(sketch);
        }
        {
            var Q0;
            Q0=makeQuery(id+"F12.imprint","IMPRINT",FACE,{"disambiguationData":[TD([[makeQuery(id+"F12.imprint","IMPRINT",EDGE,{"derivedFrom":sQuery(id+"F12.wireOp",EDGE,"E106.bottom")}),1.0]])]});
            extrude(context, id + "F13", {"entities" : qUnion([Q0]), "depth" : 12 * mm, "offsetDistance" : 25 * mm});
        }
        {
            var Q0;
            {var subQ0=sQuery(id+"F9.wireOp",EDGE,"E74.0");var subQ1=sQuery(id+"F9.wireOp",EDGE,"E54.left");var subQ2=makeQuery(id+"F9.imprint","INTERSECT",VERTEX,{"derivedFrom":[subQ1,subQ0]});Q0=makeQuery(id+"F9.imprint","IMPRINT",FACE,{"disambiguationData":[TD([[makeQuery(id+"F9.imprint","IMPRINT",EDGE,{"disambiguationData":[TD([[subQ2,-1.0]])],"derivedFrom":subQ1}),1.0]])]});}
            var Q1;
            {var subQ0=sQuery(id+"F9.wireOp",EDGE,"E62.0");var subQ1=sQuery(id+"F9.wireOp",EDGE,"E54.left");var subQ2=makeQuery(id+"F9.imprint","INTERSECT",VERTEX,{"derivedFrom":[subQ1,subQ0]});Q1=makeQuery(id+"F9.imprint","IMPRINT",FACE,{"disambiguationData":[TD([[makeQuery(id+"F9.imprint","IMPRINT",EDGE,{"disambiguationData":[TD([[subQ2,-1.0]])],"derivedFrom":subQ1}),1.0]])]});}
            var Q2;
            {var subQ0=sQuery(id+"F9.wireOp",EDGE,"E62.0");var subQ1=sQuery(id+"F9.wireOp",EDGE,"E54.right");var subQ2=makeQuery(id+"F9.imprint","INTERSECT",VERTEX,{"derivedFrom":[subQ1,subQ0]});Q2=makeQuery(id+"F9.imprint","IMPRINT",FACE,{"disambiguationData":[TD([[makeQuery(id+"F9.imprint","IMPRINT",EDGE,{"disambiguationData":[TD([[subQ2,-1.0]])],"derivedFrom":subQ1}),1.0]])]});}
            var Q3;
            {var subQ0=sQuery(id+"F9.wireOp",EDGE,"E74.0");var subQ1=sQuery(id+"F9.wireOp",EDGE,"E57.0");var subQ2=makeQuery(id+"F9.imprint","INTERSECT",VERTEX,{"derivedFrom":[subQ1,subQ0]});Q3=makeQuery(id+"F9.imprint","IMPRINT",FACE,{"disambiguationData":[TD([[makeQuery(id+"F9.imprint","IMPRINT",EDGE,{"disambiguationData":[TD([[subQ2,-1.0]])],"derivedFrom":subQ1}),1.0]])]});}
            var Q4;
            {var subQ0=sQuery(id+"F9.wireOp",EDGE,"E73.0");var subQ1=sQuery(id+"F9.wireOp",EDGE,"E57.0");var subQ2=makeQuery(id+"F9.imprint","INTERSECT",VERTEX,{"derivedFrom":[subQ1,subQ0]});Q4=makeQuery(id+"F9.imprint","IMPRINT",FACE,{"disambiguationData":[TD([[makeQuery(id+"F9.imprint","IMPRINT",EDGE,{"disambiguationData":[TD([[subQ2,-1.0]])],"derivedFrom":subQ1}),1.0]])]});}
            var Q5;
            {var subQ0=sQuery(id+"F9.wireOp",EDGE,"E74.0");var subQ1=sQuery(id+"F9.wireOp",EDGE,"E56.0");var subQ2=makeQuery(id+"F9.imprint","INTERSECT",VERTEX,{"derivedFrom":[subQ1,subQ0]});Q5=makeQuery(id+"F9.imprint","IMPRINT",FACE,{"disambiguationData":[TD([[makeQuery(id+"F9.imprint","IMPRINT",EDGE,{"disambiguationData":[TD([[subQ2,-1.0]])],"derivedFrom":subQ1}),-1.0]])]});}
            var Q6;
            {var subQ0=sQuery(id+"F9.wireOp",EDGE,"E74.0");var subQ1=sQuery(id+"F9.wireOp",EDGE,"E55.0");var subQ2=makeQuery(id+"F9.imprint","INTERSECT",VERTEX,{"derivedFrom":[subQ1,subQ0]});Q6=makeQuery(id+"F9.imprint","IMPRINT",FACE,{"disambiguationData":[TD([[makeQuery(id+"F9.imprint","IMPRINT",EDGE,{"disambiguationData":[TD([[subQ2,-1.0]])],"derivedFrom":subQ1}),1.0]])]});}
            var Q7;
            {var subQ0=sQuery(id+"F9.wireOp",EDGE,"E62.0");var subQ1=sQuery(id+"F9.wireOp",EDGE,"E42.right");var subQ2=makeQuery(id+"F9.imprint","INTERSECT",VERTEX,{"derivedFrom":[subQ1,subQ0]});Q7=makeQuery(id+"F9.imprint","IMPRINT",FACE,{"disambiguationData":[TD([[makeQuery(id+"F9.imprint","IMPRINT",EDGE,{"disambiguationData":[TD([[subQ2,1.0]])],"derivedFrom":subQ1}),1.0]])]});}
            var Q8;
            {var subQ0=sQuery(id+"F9.wireOp",EDGE,"E74.0");var subQ1=sQuery(id+"F9.wireOp",EDGE,"E42.right");var subQ2=makeQuery(id+"F9.imprint","INTERSECT",VERTEX,{"derivedFrom":[subQ1,subQ0]});Q8=makeQuery(id+"F9.imprint","IMPRINT",FACE,{"disambiguationData":[TD([[makeQuery(id+"F9.imprint","IMPRINT",EDGE,{"disambiguationData":[TD([[subQ2,1.0]])],"derivedFrom":subQ1}),1.0]])]});}
            var Q9;
            {var subQ0=sQuery(id+"F9.wireOp",EDGE,"E65");Q9=makeQuery(id+"F9.imprint","IMPRINT",FACE,{"disambiguationData":[TD([[makeQuery(id+"F9.imprint","IMPRINT",EDGE,{"derivedFrom":subQ0}),-1.0]])]});}
            var Q10;
            {var subQ0=sQuery(id+"F9.wireOp",EDGE,"E63");Q10=makeQuery(id+"F9.imprint","IMPRINT",FACE,{"disambiguationData":[TD([[makeQuery(id+"F9.imprint","IMPRINT",EDGE,{"derivedFrom":subQ0}),-1.0]])]});}
            var Q11;
            {var subQ0=sQuery(id+"F9.wireOp",EDGE,"E60");var subQ5=sQuery(id+"F9.wireOp",EDGE,"E71.0");var subQ6=makeQuery(id+"F9.imprint","INTERSECT",VERTEX,{"derivedFrom":[subQ0,subQ5]});Q11=makeQuery(id+"F9.imprint","IMPRINT",FACE,{"disambiguationData":[TD([[makeQuery(id+"F9.imprint","IMPRINT",EDGE,{"disambiguationData":[TD([[subQ6,1.0]])],"derivedFrom":subQ5}),-1.0]])]});}
            var Q12;
            {var subQ0=sQuery(id+"F9.wireOp",EDGE,"E67.0");var subQ1=sQuery(id+"F9.wireOp",EDGE,"E60");var subQ2=makeQuery(id+"F9.imprint","INTERSECT",VERTEX,{"derivedFrom":[subQ1,subQ0]});Q12=makeQuery(id+"F9.imprint","IMPRINT",FACE,{"disambiguationData":[TD([[makeQuery(id+"F9.imprint","IMPRINT",EDGE,{"disambiguationData":[TD([[subQ2,-1.0]])],"derivedFrom":subQ1}),-1.0]])]});}
            var Q13;
            {var subQ0=sQuery(id+"F9.wireOp",EDGE,"E67.0");var subQ1=sQuery(id+"F9.wireOp",EDGE,"E61.0");var subQ2=makeQuery(id+"F9.imprint","INTERSECT",VERTEX,{"derivedFrom":[subQ1,subQ0]});Q13=makeQuery(id+"F9.imprint","IMPRINT",FACE,{"disambiguationData":[TD([[makeQuery(id+"F9.imprint","IMPRINT",EDGE,{"disambiguationData":[TD([[subQ2,-1.0]])],"derivedFrom":subQ1}),-1.0]])]});}
            var Q14;
            {var subQ0=sQuery(id+"F9.wireOp",EDGE,"E70.0");var subQ1=sQuery(id+"F9.wireOp",EDGE,"E60");var subQ2=makeQuery(id+"F9.imprint","INTERSECT",VERTEX,{"derivedFrom":[subQ1,subQ0]});Q14=makeQuery(id+"F9.imprint","IMPRINT",FACE,{"disambiguationData":[TD([[makeQuery(id+"F9.imprint","IMPRINT",EDGE,{"disambiguationData":[TD([[subQ2,-1.0]])],"derivedFrom":subQ1}),-1.0]])]});}
            var Q15;
            {var subQ0=sQuery(id+"F9.wireOp",EDGE,"E70.0");var subQ1=sQuery(id+"F9.wireOp",EDGE,"E61.0");var subQ2=makeQuery(id+"F9.imprint","INTERSECT",VERTEX,{"derivedFrom":[subQ1,subQ0]});Q15=makeQuery(id+"F9.imprint","IMPRINT",FACE,{"disambiguationData":[TD([[makeQuery(id+"F9.imprint","IMPRINT",EDGE,{"disambiguationData":[TD([[subQ2,-1.0]])],"derivedFrom":subQ1}),-1.0]])]});}
            var Q16;
            {var subQ0=sQuery(id+"F9.wireOp",EDGE,"E60");var subQ1=sQuery(id+"F9.wireOp",EDGE,"E59");var subQ2=makeQuery(id+"F9.imprint","INTERSECT",VERTEX,{"derivedFrom":[subQ1,subQ0]});Q16=makeQuery(id+"F9.imprint","IMPRINT",FACE,{"disambiguationData":[TD([[makeQuery(id+"F9.imprint","IMPRINT",EDGE,{"disambiguationData":[TD([[subQ2,1.0]])],"derivedFrom":subQ1}),-1.0]])]});}
            var Q17;
            {var subQ0=sQuery(id+"F9.wireOp",EDGE,"E60");var subQ1=sQuery(id+"F9.wireOp",EDGE,"E45.left");var subQ2=makeQuery(id+"F9.imprint","INTERSECT",VERTEX,{"derivedFrom":[subQ1,subQ0]});Q17=makeQuery(id+"F9.imprint","IMPRINT",FACE,{"disambiguationData":[TD([[makeQuery(id+"F9.imprint","IMPRINT",EDGE,{"disambiguationData":[TD([[subQ2,1.0]])],"derivedFrom":subQ1}),-1.0]])]});}
            var Q18;
            {var subQ0=sQuery(id+"F9.wireOp",EDGE,"E61.0");var subQ1=sQuery(id+"F9.wireOp",EDGE,"E45.left");var subQ2=makeQuery(id+"F9.imprint","INTERSECT",VERTEX,{"derivedFrom":[subQ1,subQ0]});Q18=makeQuery(id+"F9.imprint","IMPRINT",FACE,{"disambiguationData":[TD([[makeQuery(id+"F9.imprint","IMPRINT",EDGE,{"disambiguationData":[TD([[subQ2,1.0]])],"derivedFrom":subQ1}),-1.0]])]});}
            var Q19;
            {var subQ0=sQuery(id+"F9.wireOp",EDGE,"E105");Q19=makeQuery(id+"F9.imprint","IMPRINT",FACE,{"disambiguationData":[TD([[makeQuery(id+"F9.imprint","IMPRINT",EDGE,{"derivedFrom":subQ0}),-1.0]])]});}
            var Q20;
            {var subQ0=sQuery(id+"F9.wireOp",EDGE,"E101");var subQ1=sQuery(id+"F9.wireOp",EDGE,"E56.0");var subQ2=makeQuery(id+"F9.imprint","INTERSECT",VERTEX,{"derivedFrom":[subQ1,subQ0]});Q20=makeQuery(id+"F9.imprint","IMPRINT",FACE,{"disambiguationData":[TD([[makeQuery(id+"F9.imprint","IMPRINT",EDGE,{"disambiguationData":[TD([[subQ2,-1.0]])],"derivedFrom":subQ1}),-1.0]])]});}
            var Q21;
            {var subQ0=sQuery(id+"F9.wireOp",EDGE,"E102");var subQ1=sQuery(id+"F9.wireOp",EDGE,"E56.0");var subQ2=makeQuery(id+"F9.imprint","INTERSECT",VERTEX,{"derivedFrom":[subQ1,subQ0]});Q21=makeQuery(id+"F9.imprint","IMPRINT",FACE,{"disambiguationData":[TD([[makeQuery(id+"F9.imprint","IMPRINT",EDGE,{"disambiguationData":[TD([[subQ2,-1.0]])],"derivedFrom":subQ1}),-1.0]])]});}
            var Q22;
            {var subQ3=sQuery(id+"F9.wireOp",EDGE,"E55.0");var subQ9=sQuery(id+"F9.wireOp",EDGE,"E93");var subQ11=makeQuery(id+"F9.imprint","INTERSECT",VERTEX,{"derivedFrom":[subQ3,subQ9]});Q22=makeQuery(id+"F9.imprint","IMPRINT",FACE,{"disambiguationData":[TD([[makeQuery(id+"F9.imprint","IMPRINT",EDGE,{"disambiguationData":[TD([[subQ11,-1.0]])],"derivedFrom":subQ3}),1.0]])]});}
            var Q23;
            {var subQ0=sQuery(id+"F9.wireOp",EDGE,"E92");var subQ1=sQuery(id+"F9.wireOp",EDGE,"E42.right");var subQ2=makeQuery(id+"F9.imprint","INTERSECT",VERTEX,{"derivedFrom":[subQ1,subQ0]});Q23=makeQuery(id+"F9.imprint","IMPRINT",FACE,{"disambiguationData":[TD([[makeQuery(id+"F9.imprint","IMPRINT",EDGE,{"disambiguationData":[TD([[subQ2,1.0]])],"derivedFrom":subQ1}),1.0]])]});}
            var Q24;
            {var subQ0=sQuery(id+"F9.wireOp",EDGE,"E93");var subQ1=sQuery(id+"F9.wireOp",EDGE,"E42.right");var subQ2=makeQuery(id+"F9.imprint","INTERSECT",VERTEX,{"derivedFrom":[subQ1,subQ0]});Q24=makeQuery(id+"F9.imprint","IMPRINT",FACE,{"disambiguationData":[TD([[makeQuery(id+"F9.imprint","IMPRINT",EDGE,{"disambiguationData":[TD([[subQ2,1.0]])],"derivedFrom":subQ1}),1.0]])]});}
            var Q25;
            {var subQ0=sQuery(id+"F9.wireOp",EDGE,"E66.0");var subQ1=sQuery(id+"F9.wireOp",EDGE,"E60");var subQ2=makeQuery(id+"F9.imprint","INTERSECT",VERTEX,{"derivedFrom":[subQ1,subQ0]});Q25=makeQuery(id+"F9.imprint","IMPRINT",FACE,{"disambiguationData":[TD([[makeQuery(id+"F9.imprint","IMPRINT",EDGE,{"disambiguationData":[TD([[subQ2,1.0]])],"derivedFrom":subQ1}),-1.0]])]});}
            var Q26;
            {var subQ5=sQuery(id+"F9.wireOp",EDGE,"E90");Q26=makeQuery(id+"F9.imprint","IMPRINT",FACE,{"disambiguationData":[TD([[makeQuery(id+"F9.imprint","IMPRINT",EDGE,{"derivedFrom":subQ5}),-1.0]])]});}
            var Q27;
            {var subQ0=sQuery(id+"F9.wireOp",EDGE,"E90");Q27=makeQuery(id+"F9.imprint","IMPRINT",FACE,{"disambiguationData":[TD([[makeQuery(id+"F9.imprint","IMPRINT",EDGE,{"derivedFrom":subQ0}),1.0]])]});}
            var Q28;
            {var subQ0=sQuery(id+"F9.wireOp",EDGE,"E67.0");var subQ1=sQuery(id+"F9.wireOp",EDGE,"E60");var subQ2=makeQuery(id+"F9.imprint","INTERSECT",VERTEX,{"derivedFrom":[subQ1,subQ0]});Q28=makeQuery(id+"F9.imprint","IMPRINT",FACE,{"disambiguationData":[TD([[makeQuery(id+"F9.imprint","IMPRINT",EDGE,{"disambiguationData":[TD([[subQ2,-1.0]])],"derivedFrom":subQ1}),-1.0]])]});}
            var Q29;
            {var subQ5=sQuery(id+"F9.wireOp",EDGE,"E95");Q29=makeQuery(id+"F9.imprint","IMPRINT",FACE,{"disambiguationData":[TD([[makeQuery(id+"F9.imprint","IMPRINT",EDGE,{"derivedFrom":subQ5}),1.0]])]});}
            var Q30;
            {var subQ0=sQuery(id+"F9.wireOp",EDGE,"E95");Q30=makeQuery(id+"F9.imprint","IMPRINT",FACE,{"disambiguationData":[TD([[makeQuery(id+"F9.imprint","IMPRINT",EDGE,{"derivedFrom":subQ0}),-1.0]])]});}
            var Q31;
            {var subQ0=sQuery(id+"F9.wireOp",EDGE,"E96");Q31=makeQuery(id+"F9.imprint","IMPRINT",FACE,{"disambiguationData":[TD([[makeQuery(id+"F9.imprint","IMPRINT",EDGE,{"derivedFrom":subQ0}),-1.0]])]});}
            var Q32;
            {var subQ0=sQuery(id+"F9.wireOp",EDGE,"E65");Q32=makeQuery(id+"F9.imprint","IMPRINT",FACE,{"disambiguationData":[TD([[makeQuery(id+"F9.imprint","IMPRINT",EDGE,{"derivedFrom":subQ0}),-1.0]])]});}
            var Q33;
            {var subQ0=sQuery(id+"F9.wireOp",EDGE,"E60");var subQ1=sQuery(id+"F9.wireOp",EDGE,"E45.left");var subQ2=makeQuery(id+"F9.imprint","INTERSECT",VERTEX,{"derivedFrom":[subQ1,subQ0]});Q33=makeQuery(id+"F9.imprint","IMPRINT",FACE,{"disambiguationData":[TD([[makeQuery(id+"F9.imprint","IMPRINT",EDGE,{"disambiguationData":[TD([[subQ2,1.0]])],"derivedFrom":subQ1}),-1.0]])]});}
            var Q34;
            {var subQ0=sQuery(id+"F9.wireOp",EDGE,"E91");Q34=makeQuery(id+"F9.imprint","IMPRINT",FACE,{"disambiguationData":[TD([[makeQuery(id+"F9.imprint","IMPRINT",EDGE,{"derivedFrom":subQ0}),1.0]])]});}
            var Q35;
            {var subQ3=sQuery(id+"F9.wireOp",EDGE,"E91");Q35=makeQuery(id+"F9.imprint","IMPRINT",FACE,{"disambiguationData":[TD([[makeQuery(id+"F9.imprint","IMPRINT",EDGE,{"derivedFrom":subQ3}),-1.0]])]});}
            extrude(context, id + "F14", {"entities" : qUnion([Q0, Q1, Q2, Q3, Q4, Q5, Q6, Q7, Q8, Q9, Q10, Q11, Q12, Q13, Q14, Q15, Q16, Q17, Q18, Q19, Q20, Q21, Q22, Q23, Q24, Q25, Q26, Q27, Q28, Q29, Q30, Q31, Q32, Q33, Q34, Q35]), "depth" : 400 * mm, "offsetDistance" : 25 * mm});
        }
        {
            var Q0;
            Q0=makeQuery(id+"F14.opExtrude","SWEPT_FACE",FACE,{"disambiguationData":[OSD([sQuery(id+"F9.wireOp",EDGE,"E93")])]});
            var sketch = newSketch(context, id + "F15", { "sketchPlane" : qUnion([Q0])});
            skLineSegment(sketch, "E107.bottom", {"start": v(964, 0) * mm, "end": v(478.5, 0) * mm});
            skLineSegment(sketch, "E107.top", {"start": v(964, 15) * mm, "end": v(478.5, 15) * mm});
            skLineSegment(sketch, "E107.left", {"start": v(964, 0) * mm, "end": v(964, 15) * mm});
            skLineSegment(sketch, "E107.right", {"start": v(478.5, 0) * mm, "end": v(478.5, 15) * mm});
            skSolve(sketch);
        }
        {
            var Q0;
            {var subQ0=sQuery(id+"F15.wireOp",EDGE,"E107.bottom");var subQ1=makeQuery(id+"F14.opExtrude","SWEPT_EDGE",EDGE,{"disambiguationData":[OSD([sQuery(id+"F9.wireOp",EDGE,"E55.0"),sQuery(id+"F9.wireOp",EDGE,"E93")])]});var subQ2=makeQuery(id+"F15.imprint","INTERSECT",VERTEX,{"derivedFrom":[subQ1,subQ0]});Q0=makeQuery(id+"F15.imprint","IMPRINT",FACE,{"disambiguationData":[TD([[makeQuery(id+"F15.imprint","IMPRINT",EDGE,{"disambiguationData":[TD([[subQ2,-1.0]])],"derivedFrom":subQ0}),-1.0]])]});}
            var Q1;
            {var subQ3=sQuery(id+"F15.wireOp",EDGE,"E107.right");Q1=makeQuery(id+"F15.imprint","IMPRINT",FACE,{"disambiguationData":[TD([[makeQuery(id+"F15.imprint","IMPRINT",EDGE,{"derivedFrom":subQ3}),-1.0]])]});}
            var Q2;
            {var subQ3=sQuery(id+"F15.wireOp",EDGE,"E107.left");Q2=makeQuery(id+"F15.imprint","IMPRINT",FACE,{"disambiguationData":[TD([[makeQuery(id+"F15.imprint","IMPRINT",EDGE,{"derivedFrom":subQ3}),1.0]])]});}
            var Q3;
            Q3=makeQuery(id+"F14.opExtrude","SWEPT_FACE",FACE,{"disambiguationData":[OSD([sQuery(id+"F9.wireOp",EDGE,"E94")])]});
            var Q4;
            Q4=makeQuery(id+"F14.opExtrude","SWEPT_FACE",FACE,{"disambiguationData":[OSD([sQuery(id+"F9.wireOp",EDGE,"E92"),sQuery(id+"F9.wireOp",EDGE,"E103")])]});
            extrude(context, id + "F16", {"entities" : qUnion([Q0, Q1, Q2]), "endBound" : BoundingType.UP_TO_SURFACE, "depth" : 25 * mm, "endBoundEntityFace" : qUnion([Q3]), "offsetDistance" : 25 * mm, "hasSecondDirection" : true, "secondDirectionBound" : SecondDirectionBoundingType.UP_TO_SURFACE, "secondDirectionOppositeDirection" : true, "secondDirectionDepth" : 25 * mm, "secondDirectionBoundEntityFace" : qUnion([Q4])});
        }
        {
            var Q0;
            Q0=makeQuery(id+"F16.opExtrude","SWEPT_BODY",BODY,{"disambiguationData":[OSD([sQuery(id+"F15.wireOp",EDGE,"E107.bottom"),sQuery(id+"F15.wireOp",EDGE,"E107.top"),sQuery(id+"F15.wireOp",EDGE,"E107.left"),sQuery(id+"F15.wireOp",EDGE,"E107.right")])]});
            var Q1;
            Q1=makeQuery(id+"F14.opExtrude","SWEPT_BODY",BODY,{"disambiguationData":[OSD([sQuery(id+"F9.wireOp",EDGE,"E42.right"),sQuery(id+"F9.wireOp",EDGE,"E55.0"),sQuery(id+"F9.wireOp",EDGE,"E56.0"),sQuery(id+"F9.wireOp",EDGE,"E69.0"),sQuery(id+"F9.wireOp",EDGE,"E92"),sQuery(id+"F9.wireOp",EDGE,"E93"),sQuery(id+"F9.wireOp",EDGE,"E94"),sQuery(id+"F9.wireOp",EDGE,"E101"),sQuery(id+"F9.wireOp",EDGE,"E102"),sQuery(id+"F9.wireOp",EDGE,"E103")])]});
            booleanBodies(context, id + "F17", {"operationType" : BooleanOperationType.SUBTRACTION, "tools" : qUnion([Q0]), "targets" : qUnion([Q1]), "keepTools" : true});
        }
        {
            var Q0;
            Q0=makeQuery(id+"F8.opExtrude","CAP_FACE",FACE,{"disambiguationData":[OSD([sQuery(id+"F7.wireOp",EDGE,"E14.top"),sQuery(id+"F7.wireOp",EDGE,"E14.left"),sQuery(id+"F7.wireOp",EDGE,"E14.right"),sQuery(id+"F7.wireOp",EDGE,"E39")])],"isStart":true});
            var sketch = newSketch(context, id + "F18", { "sketchPlane" : qUnion([Q0])});
            skLineSegment(sketch, "E108.bottom", {"start": v(-51, 666) * mm, "end": v(-653, 666) * mm});
            skLineSegment(sketch, "E108.top", {"start": v(-51, 654) * mm, "end": v(-653, 654) * mm});
            skLineSegment(sketch, "E108.left", {"start": v(-51, 666) * mm, "end": v(-51, 654) * mm});
            skLineSegment(sketch, "E108.right", {"start": v(-653, 666) * mm, "end": v(-653, 654) * mm});
            skLineSegment(sketch, "E109", {"start": v(-51, 654) * mm, "end": v(-51, 613) * mm});
            skLineSegment(sketch, "E110", {"start": v(-51, 613) * mm, "end": v(-653, 613) * mm});
            skLineSegment(sketch, "E111", {"start": v(-653, 613) * mm, "end": v(-653, 654) * mm});
            skLineSegment(sketch, "E112.0", {"start": v(-51, 623) * mm, "end": v(-653, 623) * mm});
            skLineSegment(sketch, "E113.0", {"start": v(-63, 654) * mm, "end": v(-63, 613) * mm});
            skLineSegment(sketch, "E114.0", {"start": v(-641, 613) * mm, "end": v(-641, 654) * mm});
            skLineSegment(sketch, "E115", {"start": v(-51, 654) * mm, "end": v(-36, 654) * mm});
            skLineSegment(sketch, "E116", {"start": v(-653, 654) * mm, "end": v(-668, 654) * mm});
            skLineSegment(sketch, "E117", {"start": v(-36, 654) * mm, "end": v(-36, 666) * mm});
            skLineSegment(sketch, "E118", {"start": v(-36, 666) * mm, "end": v(-51, 666) * mm});
            skLineSegment(sketch, "E119", {"start": v(-668, 654) * mm, "end": v(-668, 666) * mm});
            skLineSegment(sketch, "E120", {"start": v(-668, 666) * mm, "end": v(-653, 666) * mm});
            skSolve(sketch);
        }
        {
            var Q0;
            {var subQ0=sQuery(id+"F18.wireOp",EDGE,"E109");var subQ5=sQuery(id+"F18.wireOp",EDGE,"E112.0");var subQ6=makeQuery(id+"F18.imprint","INTERSECT",VERTEX,{"derivedFrom":[subQ0,subQ5]});Q0=makeQuery(id+"F18.imprint","IMPRINT",FACE,{"disambiguationData":[TD([[makeQuery(id+"F18.imprint","IMPRINT",EDGE,{"disambiguationData":[TD([[subQ6,-1.0]])],"derivedFrom":subQ5}),-1.0]])]});}
            var Q1;
            {var subQ0=sQuery(id+"F18.wireOp",EDGE,"E110");var subQ1=sQuery(id+"F18.wireOp",EDGE,"E109");var subQ2=makeQuery(id+"F18.imprint","INTERSECT",VERTEX,{"derivedFrom":[subQ1,subQ0]});Q1=makeQuery(id+"F18.imprint","IMPRINT",FACE,{"disambiguationData":[TD([[makeQuery(id+"F18.imprint","IMPRINT",EDGE,{"disambiguationData":[TD([[subQ2,1.0]])],"derivedFrom":subQ1}),-1.0]])]});}
            var Q2;
            {var subQ0=sQuery(id+"F18.wireOp",EDGE,"E113.0");var subQ1=sQuery(id+"F18.wireOp",EDGE,"E110");var subQ2=makeQuery(id+"F18.imprint","INTERSECT",VERTEX,{"derivedFrom":[subQ1,subQ0]});Q2=makeQuery(id+"F18.imprint","IMPRINT",FACE,{"disambiguationData":[TD([[makeQuery(id+"F18.imprint","IMPRINT",EDGE,{"disambiguationData":[TD([[subQ2,-1.0]])],"derivedFrom":subQ1}),-1.0]])]});}
            var Q3;
            {var subQ0=sQuery(id+"F18.wireOp",EDGE,"E111");var subQ1=sQuery(id+"F18.wireOp",EDGE,"E110");var subQ2=makeQuery(id+"F18.imprint","INTERSECT",VERTEX,{"derivedFrom":[subQ1,subQ0]});Q3=makeQuery(id+"F18.imprint","IMPRINT",FACE,{"disambiguationData":[TD([[makeQuery(id+"F18.imprint","IMPRINT",EDGE,{"disambiguationData":[TD([[subQ2,1.0]])],"derivedFrom":subQ1}),-1.0]])]});}
            var Q4;
            {var subQ0=sQuery(id+"F18.wireOp",EDGE,"E111");var subQ5=sQuery(id+"F18.wireOp",EDGE,"E112.0");var subQ6=makeQuery(id+"F18.imprint","INTERSECT",VERTEX,{"derivedFrom":[subQ0,subQ5]});Q4=makeQuery(id+"F18.imprint","IMPRINT",FACE,{"disambiguationData":[TD([[makeQuery(id+"F18.imprint","IMPRINT",EDGE,{"disambiguationData":[TD([[subQ6,1.0]])],"derivedFrom":subQ5}),-1.0]])]});}
            extrude(context, id + "F19", {"entities" : qUnion([Q0, Q1, Q2, Q3, Q4]), "depth" : 380 * mm, "offsetDistance" : 25 * mm});
        }
        {
            var Q0;
            Q0=makeQuery(id+"F19.opExtrude","SWEPT_FACE",FACE,{"disambiguationData":[OSD([sQuery(id+"F18.wireOp",EDGE,"E112.0")])]});
            var sketch = newSketch(context, id + "F20", { "sketchPlane" : qUnion([Q0])});
            skLineSegment(sketch, "E121.bottom", {"start": v(63, 380) * mm, "end": v(641, 380) * mm});
            skLineSegment(sketch, "E121.top", {"start": v(63, 368) * mm, "end": v(641, 368) * mm});
            skLineSegment(sketch, "E121.left", {"start": v(63, 380) * mm, "end": v(63, 368) * mm});
            skLineSegment(sketch, "E121.right", {"start": v(641, 380) * mm, "end": v(641, 368) * mm});
            skSolve(sketch);
        }
        {
            var Q0;
            Q0=makeQuery(id+"F20.imprint","IMPRINT",FACE,{"disambiguationData":[TD([[makeQuery(id+"F20.imprint","IMPRINT",EDGE,{"derivedFrom":sQuery(id+"F20.wireOp",EDGE,"E121.bottom")}),-1.0]])]});
            var Q1;
            {var subQ0=sQuery(id+"F18.wireOp",EDGE,"E108.top");Q1=makeQuery(id+"F19.opExtrude","SWEPT_FACE",FACE,{"disambiguationData":[OSD([subQ0]),TDD([makeQuery(id+"F18.imprint","IMPRINT",EDGE,{"disambiguationData":[TD([[makeQuery(id+"F18.imprint","INTERSECT",VERTEX,{"derivedFrom":[subQ0,sQuery(id+"F18.wireOp",EDGE,"E114.0")]}),-1.0]])],"derivedFrom":subQ0})])]});}
            extrude(context, id + "F21", {"entities" : qUnion([Q0]), "endBound" : BoundingType.UP_TO_SURFACE, "depth" : 25 * mm, "endBoundEntityFace" : qUnion([Q1]), "offsetDistance" : 25 * mm});
        }
        {
            var Q0;
            Q0=makeQuery(id+"F8.opExtrude","SWEPT_FACE",FACE,{"disambiguationData":[OSD([sQuery(id+"F7.wireOp",EDGE,"E14.right")])]});
            var Q1;
            Q1=makeQuery(id+"F11.opExtrude","SWEPT_FACE",FACE,{"disambiguationData":[OSD([sQuery(id+"F9.wireOp",EDGE,"E51.left")])]});
            extrude(context, id + "F22", {"entities" : qUnion([Q0]), "operationType" : NewBodyOperationType.ADD, "endBound" : BoundingType.UP_TO_SURFACE, "depth" : 25 * mm, "endBoundEntityFace" : qUnion([Q1]), "offsetDistance" : 25 * mm});
        }
        {
            var Q0;
            Q0=makeQuery(id+"F18.imprint","IMPRINT",FACE,{"disambiguationData":[TD([[makeQuery(id+"F18.imprint","IMPRINT",EDGE,{"derivedFrom":sQuery(id+"F18.wireOp",EDGE,"E108.bottom")}),1.0]])]});
            var Q1;
            Q1=makeQuery(id+"F18.imprint","IMPRINT",FACE,{"disambiguationData":[TD([[makeQuery(id+"F18.imprint","IMPRINT",EDGE,{"derivedFrom":sQuery(id+"F18.wireOp",EDGE,"E108.right")}),-1.0]])]});
            var Q2;
            Q2=makeQuery(id+"F18.imprint","IMPRINT",FACE,{"disambiguationData":[TD([[makeQuery(id+"F18.imprint","IMPRINT",EDGE,{"derivedFrom":sQuery(id+"F18.wireOp",EDGE,"E108.left")}),1.0]])]});
            var Q3;
            Q3=makeQuery(id+"F21.opExtrude","SWEPT_FACE",FACE,{"disambiguationData":[OSD([sQuery(id+"F20.wireOp",EDGE,"E121.bottom")])]});
            extrude(context, id + "F23", {"entities" : qUnion([Q0, Q1, Q2]), "endBound" : BoundingType.UP_TO_SURFACE, "depth" : 25 * mm, "endBoundEntityFace" : qUnion([Q3]), "offsetDistance" : 25 * mm});
        }
        {
            var Q0;
            Q0=makeQuery(id+"F23.opExtrude","SWEPT_FACE",FACE,{"disambiguationData":[OSD([sQuery(id+"F18.wireOp",EDGE,"E108.bottom"),sQuery(id+"F18.wireOp",EDGE,"E118"),sQuery(id+"F18.wireOp",EDGE,"E120")])]});
            var sketch = newSketch(context, id + "F24", { "sketchPlane" : qUnion([Q0])});
            skLineSegment(sketch, "E122.bottom", {"start": v(36, 380) * mm, "end": v(668, 380) * mm});
            skLineSegment(sketch, "E122.top", {"start": v(36, 300) * mm, "end": v(668, 300) * mm});
            skLineSegment(sketch, "E122.left", {"start": v(36, 380) * mm, "end": v(36, 300) * mm});
            skLineSegment(sketch, "E122.right", {"start": v(668, 380) * mm, "end": v(668, 300) * mm});
            skLineSegment(sketch, "E123.0", {"start": v(36, 368) * mm, "end": v(668, 368) * mm});
            skSolve(sketch);
        }
        {
            var Q0;
            {var subQ0=sQuery(id+"F24.wireOp",EDGE,"E122.bottom");Q0=makeQuery(id+"F24.imprint","IMPRINT",FACE,{"disambiguationData":[TD([[makeQuery(id+"F24.imprint","IMPRINT",EDGE,{"derivedFrom":subQ0}),-1.0]])]});}
            var Q1;
            Q1=makeQuery(id+"F11.opExtrude","SWEPT_FACE",FACE,{"disambiguationData":[OSD([sQuery(id+"F9.wireOp",EDGE,"E98.top")])]});
            extrude(context, id + "F25", {"entities" : qUnion([Q0]), "endBound" : BoundingType.UP_TO_SURFACE, "depth" : 25 * mm, "endBoundEntityFace" : qUnion([Q1]), "offsetDistance" : 25 * mm});
        }
    });
